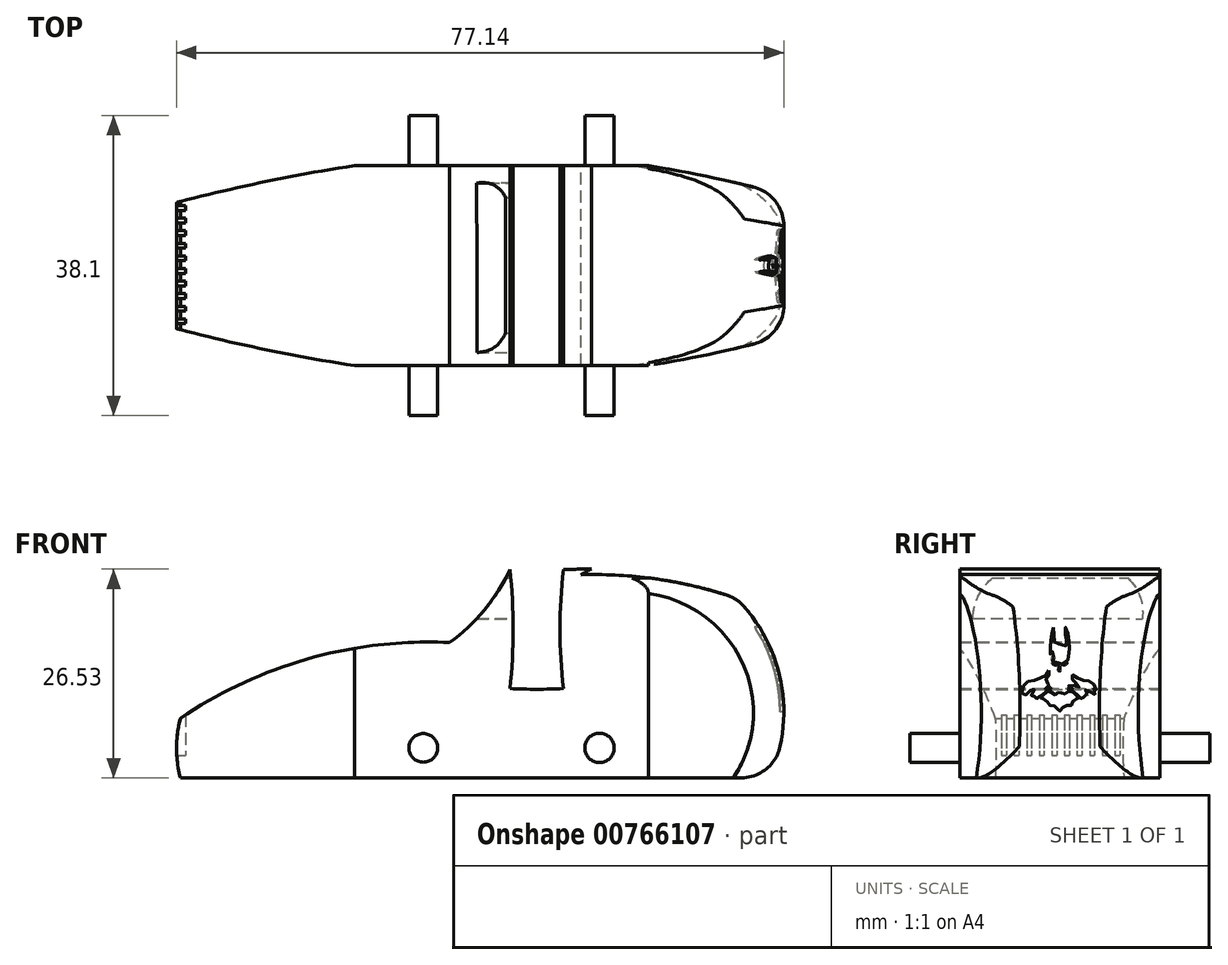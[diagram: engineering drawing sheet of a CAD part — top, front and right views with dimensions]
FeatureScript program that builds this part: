
annotation { "Feature Type Name" : "Feature", "Feature Type Description" : "" }
export const myFeature = defineFeature(function(context is Context, id is Id, definition is map)
    precondition{}
    {
        {
            var Q0;
            Q0=qCreatedBy(makeId("Front.planeOp"),FACE);
            var sketch = newSketch(context, id + "F0", { "sketchPlane" : qUnion([Q0])});
            skLineSegment(sketch, "E0", {"start": v(14.06, 0) * mm, "end": v(-22.7, 0) * mm});
            skLineSegment(sketch, "E1", {"start": v(-22.7, 0) * mm, "end": v(-22.7, 4.32) * mm});
            skArc(sketch, "E2", {"start": v(-6.24, 12.14) * mm, "mid": v(-14.95, 9.24) * mm, "end": v(-22.7, 4.32) * mm});
            skArc(sketch, "E3", {"start": v(-6.24, 12.14) * mm, "mid": v(-3.82, 13.42) * mm, "end": v(-2.13, 15.57) * mm});
            skLineSegment(sketch, "E4", {"start": v(-2.13, 15.57) * mm, "end": v(0, 6.38) * mm});
            skLineSegment(sketch, "E5", {"start": v(0, 6.38) * mm, "end": v(6.51, 6.38) * mm});
            skLineSegment(sketch, "E6", {"start": v(6.51, 6.38) * mm, "end": v(6.51, 15.57) * mm});
            skArc(sketch, "E7", {"start": v(14.06, 0) * mm, "mid": v(14.06, 9.61) * mm, "end": v(6.51, 15.57) * mm});
            skCircle(sketch, "E8", {"center": v(-14.41, 3.81) * mm, "radius": 1.82 * mm});
            skCircle(sketch, "E9", {"center": v(7.97, 3.81) * mm, "radius": 1.86 * mm});
            skSolve(sketch);
        }
        {
            var Q0;
            Q0 = qSketchRegion(id + "F0", true);
            extrude(context, id + "F1", {"entities" : qUnion([Q0]), "endBound" : BoundingType.SYMMETRIC, "depth" : 17.78 * mm, "offsetDistance" : 25.4 * mm});
        }
        {
            var Q0;
            Q0=qCreatedBy(makeId("Top.planeOp"),FACE);
            var sketch = newSketch(context, id + "F2", { "sketchPlane" : qUnion([Q0])});
            skArc(sketch, "E10", {"start": v(0, 11.7) * mm, "mid": v(-18.06, 8.8) * mm, "end": v(-34.94, 1.75) * mm});
            skArc(sketch, "E11", {"start": v(21.66, 0) * mm, "mid": v(12.6, 9.1) * mm, "end": v(0, 11.7) * mm});
            skArc(sketch, "E12.MirrorCS", {"start": v(21.66, 0) * mm, "mid": v(12.6, -9.1) * mm, "end": v(0, -11.7) * mm});
            skArc(sketch, "E13.MirrorCS", {"start": v(0, -11.7) * mm, "mid": v(-18.06, -8.8) * mm, "end": v(-34.94, -1.75) * mm});
            skLineSegment(sketch, "E14", {"start": v(-34.94, -1.75) * mm, "end": v(-25.16, -25.9) * mm});
            skLineSegment(sketch, "E15", {"start": v(-25.16, -25.9) * mm, "end": v(27.75, -24.43) * mm});
            skLineSegment(sketch, "E16", {"start": v(27.75, -24.43) * mm, "end": v(34.75, 13.37) * mm});
            skLineSegment(sketch, "E17", {"start": v(34.75, 13.37) * mm, "end": v(1.57, 21.1) * mm});
            skLineSegment(sketch, "E18", {"start": v(1.57, 21.1) * mm, "end": v(-34.94, 12.44) * mm});
            skLineSegment(sketch, "E19", {"start": v(-34.94, 12.44) * mm, "end": v(-34.94, 1.75) * mm});
            skSolve(sketch);
        }
        {
            var Q0;
            Q0 = qSketchRegion(id + "F2", true);
            extrude(context, id + "F3", {"entities" : qUnion([Q0]), "operationType" : NewBodyOperationType.REMOVE, "depth" : 43.18 * mm, "offsetDistance" : 25.4 * mm});
        }
        {
            var Q0;
            Q0=makeQuery(id+"F1.opExtrude","SWEPT_BODY",BODY,{"disambiguationData":[OSD([sQuery(id+"F0.wireOp",EDGE,"E0"),sQuery(id+"F0.wireOp",EDGE,"E1"),sQuery(id+"F0.wireOp",EDGE,"E2"),sQuery(id+"F0.wireOp",EDGE,"E3"),sQuery(id+"F0.wireOp",EDGE,"E4"),sQuery(id+"F0.wireOp",EDGE,"E5"),sQuery(id+"F0.wireOp",EDGE,"E6"),sQuery(id+"F0.wireOp",EDGE,"E7")])]});
            deleteBodies(context, id + "F4", {"entities" : qUnion([Q0])});
        }
        {
            var Q0;
            Q0=qCreatedBy(makeId("Front.planeOp"),FACE);
            var sketch = newSketch(context, id + "F5", { "sketchPlane" : qUnion([Q0])});
            skArc(sketch, "E20", {"start": v(-11.07, 17.2) * mm, "mid": v(-28.95, 15.15) * mm, "end": v(-45.26, 7.56) * mm});
            skArc(sketch, "E21", {"start": v(-11.07, 17.2) * mm, "mid": v(-6.65, 21.34) * mm, "end": v(-3.41, 26.45) * mm});
            skArc(sketch, "E22", {"start": v(-3.41, 11.34) * mm, "mid": v(-3, 18.9) * mm, "end": v(-3.41, 26.45) * mm});
            skArc(sketch, "E23", {"start": v(-3.41, 11.34) * mm, "mid": v(0, 11.26) * mm, "end": v(3.41, 11.34) * mm});
            skArc(sketch, "E24", {"start": v(3.41, 26.45) * mm, "mid": v(2.95, 18.9) * mm, "end": v(3.41, 11.34) * mm});
            skArc(sketch, "E25", {"start": v(22.77, 24.98) * mm, "mid": v(13.13, 26.29) * mm, "end": v(3.41, 26.45) * mm});
            skArc(sketch, "E26", {"start": v(-45.26, 7.56) * mm, "mid": v(-45.76, 3.78) * mm, "end": v(-45.26, 0) * mm});
            skArc(sketch, "E27", {"start": v(29.59, 0) * mm, "mid": v(30.66, 13.71) * mm, "end": v(22.77, 24.98) * mm});
            skLineSegment(sketch, "E28", {"start": v(-45.26, 0) * mm, "end": v(29.59, 0) * mm});
            skLineSegment(sketch, "E29", {"start": v(-3.41, 11.34) * mm, "end": v(0, 0) * mm, "construction": true});
            skLineSegment(sketch, "E30", {"start": v(0, 0) * mm, "end": v(3.41, 11.34) * mm, "construction": true});
            skSolve(sketch);
        }
        {
            var Q0;
            Q0=makeQuery(id+"F5.imprint","IMPRINT",FACE,{"disambiguationData":[TD([[makeQuery(id+"F5.imprint","IMPRINT",EDGE,{"derivedFrom":sQuery(id+"F5.wireOp",EDGE,"E20")}),1.0]])]});
            extrude(context, id + "F6", {"entities" : qUnion([Q0]), "endBound" : BoundingType.SYMMETRIC, "depth" : 25.4 * mm, "offsetDistance" : 25.4 * mm});
        }
        {
            var Q0;
            Q0=qCreatedBy(makeId("Top.planeOp"),FACE);
            var sketch = newSketch(context, id + "F7", { "sketchPlane" : qUnion([Q0])});
            skArc(sketch, "E31", {"start": v(-5.44, 14.66) * mm, "mid": v(-27.48, 12) * mm, "end": v(-49.13, 7.1) * mm});
            skArc(sketch, "E32", {"start": v(38.25, 6.91) * mm, "mid": v(16.67, 12.28) * mm, "end": v(-5.44, 14.66) * mm});
            skArc(sketch, "E33.MirrorCS", {"start": v(38.25, -6.91) * mm, "mid": v(16.67, -12.28) * mm, "end": v(-5.44, -14.66) * mm});
            skArc(sketch, "E34.MirrorCS", {"start": v(-5.44, -14.66) * mm, "mid": v(-27.48, -12) * mm, "end": v(-49.13, -7.1) * mm});
            skLineSegment(sketch, "E35", {"start": v(-50.05, 21.85) * mm, "end": v(24.06, 21.85) * mm});
            skLineSegment(sketch, "E36", {"start": v(24.06, 21.85) * mm, "end": v(58.53, 12.81) * mm});
            skLineSegment(sketch, "E37", {"start": v(58.53, 12.81) * mm, "end": v(58.53, -6.36) * mm});
            skLineSegment(sketch, "E38", {"start": v(58.53, -6.36) * mm, "end": v(36.23, -29.4) * mm});
            skLineSegment(sketch, "E39", {"start": v(36.23, -29.4) * mm, "end": v(-53.37, -29.4) * mm});
            skLineSegment(sketch, "E40", {"start": v(-53.37, -29.4) * mm, "end": v(-69.96, 0) * mm});
            skLineSegment(sketch, "E41", {"start": v(-69.96, 0) * mm, "end": v(-50.05, 21.85) * mm});
            skLineSegment(sketch, "E42", {"start": v(-49.13, 7.1) * mm, "end": v(-49.13, -7.1) * mm});
            skLineSegment(sketch, "E43", {"start": v(38.25, 6.91) * mm, "end": v(38.25, -6.91) * mm});
            skSolve(sketch);
        }
        {
            var Q0;
            Q0=makeQuery(id+"F7.imprint","IMPRINT",FACE,{"disambiguationData":[TD([[makeQuery(id+"F7.imprint","IMPRINT",EDGE,{"derivedFrom":sQuery(id+"F7.wireOp",EDGE,"E31")}),-1.0]])]});
            extrude(context, id + "F8", {"entities" : qUnion([Q0]), "operationType" : NewBodyOperationType.REMOVE, "depth" : 25.4 * mm, "offsetDistance" : 25.4 * mm});
        }
        {
            var Q0;
            Q0=makeQuery(id+"F0.imprint","IMPRINT",FACE,{"disambiguationData":[TD([[makeQuery(id+"F0.imprint","IMPRINT",EDGE,{"derivedFrom":sQuery(id+"F0.wireOp",EDGE,"E9")}),1.0]])]});
            var Q1;
            Q1=makeQuery(id+"F0.imprint","IMPRINT",FACE,{"disambiguationData":[TD([[makeQuery(id+"F0.imprint","IMPRINT",EDGE,{"derivedFrom":sQuery(id+"F0.wireOp",EDGE,"E8")}),1.0]])]});
            extrude(context, id + "F9", {"entities" : qUnion([Q0, Q1]), "operationType" : NewBodyOperationType.ADD, "endBound" : BoundingType.SYMMETRIC, "depth" : 38.1 * mm, "offsetDistance" : 25.4 * mm});
        }
        {
            var Q0;
            Q0=qCreatedBy(makeId("Right.planeOp"),FACE);
            var sketch = newSketch(context, id + "F10", { "sketchPlane" : qUnion([Q0])});
            skArc(sketch, "E44", {"start": v(10.48, 20.22) * mm, "mid": v(10.2, 23.02) * mm, "end": v(8.66, 25.37) * mm});
            skArc(sketch, "E45", {"start": v(-8.55, 25.37) * mm, "mid": v(-10.34, 23.1) * mm, "end": v(-11.03, 20.28) * mm});
            skLineSegment(sketch, "E46", {"start": v(8.66, 25.37) * mm, "end": v(-8.55, 25.37) * mm});
            skLineSegment(sketch, "E47", {"start": v(10.48, 20.22) * mm, "end": v(-11.03, 20.28) * mm});
            skSolve(sketch);
        }
        {
            var Q0;
            Q0=makeQuery(id+"F10.imprint","IMPRINT",FACE,{"disambiguationData":[TD([[makeQuery(id+"F10.imprint","IMPRINT",EDGE,{"derivedFrom":sQuery(id+"F10.wireOp",EDGE,"E44")}),1.0]])]});
            extrude(context, id + "F11", {"entities" : qUnion([Q0]), "operationType" : NewBodyOperationType.REMOVE, "oppositeDirection" : true, "depth" : 7.65 * mm, "offsetDistance" : 25.4 * mm});
        }
        {
            var Q0;
            Q0=qCreatedBy(makeId("Right.planeOp"),FACE);
            var sketch = newSketch(context, id + "F12", { "sketchPlane" : qUnion([Q0])});
            skFitSpline(sketch, "E48", {"points": [v(-0.82, 19.14) * mm, v(-0.88, 19.02) * mm, v(-0.93, 18.82) * mm, v(-0.98, 18.55) * mm, v(-1.04, 18.17) * mm, v(-1.1, 17.77) * mm, v(-1.15, 17.25) * mm, v(-1.18, 16.87) * mm, v(-1.21, 16.4) * mm, v(-1.24, 15.96) * mm, v(-1.1, 15.47) * mm, v(-1.02, 15.47) * mm, v(-1, 15.57) * mm, v(-0.93, 15.95) * mm, v(-0.9, 16.05) * mm, v(-0.9, 15.74) * mm, v(-0.89, 15.43) * mm, v(-0.82, 15.34) * mm, v(-0.74, 15.1) * mm, v(-0.95, 15.18) * mm, v(-1.03, 15.17) * mm, v(-1.04, 14.83) * mm, v(-0.94, 14.78) * mm, v(-0.55, 14.58) * mm, v(-0.3, 14.47) * mm, v(-0.16, 14.47) * mm, v(-0.15, 14.64) * mm, v(-0.07, 14.6) * mm, v(0, 14.56) * mm, v(0.07, 14.58) * mm, v(0.07, 14.71) * mm, v(0.13, 14.73) * mm, v(0.17, 14.46) * mm, v(0.36, 14.55) * mm, v(0.64, 14.72) * mm, v(1.02, 14.83) * mm, v(1.03, 15.1) * mm, v(1.1, 15.43) * mm, v(1.17, 15.68) * mm, v(1.13, 16) * mm, v(1.08, 16.14) * mm, v(1.05, 16.2) * mm, v(1.05, 16.32) * mm, v(1.07, 16.35) * mm, v(1.11, 16.33) * mm, v(1.13, 16.27) * mm, v(1.2, 16.19) * mm, v(1.25, 16.2) * mm, v(1.25, 16.36) * mm, v(1.2, 17.1) * mm, v(1.16, 17.6) * mm, v(1.05, 18.23) * mm, v(0.89, 18.87) * mm, v(0.77, 19.15) * mm, v(0.74, 19.16) * mm, v(0.74, 18.89) * mm, v(0.74, 17.91) * mm, v(0.74, 17.66) * mm, v(0.73, 17.52) * mm, v(0.75, 17.44) * mm, v(0.82, 17.44) * mm, v(0.85, 17.54) * mm, v(0.85, 17.62) * mm, v(0.87, 17.74) * mm, v(0.88, 17.87) * mm, v(0.86, 18.02) * mm, v(0.88, 18.11) * mm, v(0.93, 18.02) * mm, v(0.93, 17.9) * mm, v(0.94, 17.73) * mm, v(0.92, 17.57) * mm, v(0.9, 17.4) * mm, v(0.9, 17.24) * mm, v(0.89, 17.1) * mm, v(0.78, 16.73) * mm, v(0.77, 16.68) * mm, v(0.56, 16.86) * mm, v(0.32, 16.97) * mm, v(0, 17.02) * mm, v(-0.31, 17) * mm, v(-0.63, 16.88) * mm, v(-0.67, 17.49) * mm, v(-0.7, 18.14) * mm, v(-0.82, 19.14) * mm]});
            skFitSpline(sketch, "E49", {"points": [v(-0.9, 14.63) * mm, v(-0.93, 14.6) * mm, v(-0.9, 14.53) * mm, v(-0.83, 14.44) * mm, v(-0.79, 14.4) * mm, v(-0.7, 14.36) * mm, v(-0.59, 14.35) * mm, v(-0.53, 14.36) * mm, v(-0.5, 14.32) * mm, v(-0.44, 14.3) * mm, v(-0.4, 14.36) * mm, v(-0.4, 14.43) * mm, v(-0.41, 14.45) * mm, v(-0.48, 14.46) * mm, v(-0.55, 14.5) * mm, v(-0.66, 14.56) * mm, v(-0.84, 14.65) * mm, v(-0.9, 14.63) * mm]});
            skFitSpline(sketch, "E50", {"points": [v(0, 14.23) * mm, v(-0.07, 14.21) * mm, v(-0.07, 14.1) * mm, v(-0.12, 13.98) * mm, v(-0.12, 13.9) * mm, v(-0.16, 13.83) * mm, v(-0.17, 13.77) * mm, v(-0.17, 13.71) * mm, v(-0.16, 13.66) * mm, v(-0.12, 13.6) * mm, v(-0.07, 13.57) * mm, v(0.04, 13.56) * mm, v(0.06, 13.6) * mm, v(0.06, 13.7) * mm, v(0.04, 13.76) * mm, v(0.04, 13.83) * mm, v(0.04, 13.93) * mm, v(0.04, 13.99) * mm, v(0.04, 14.1) * mm, v(0.04, 14.15) * mm, v(0.04, 14.2) * mm, v(0, 14.23) * mm]});
            skFitSpline(sketch, "E51", {"points": [v(0.36, 14.38) * mm, v(0.4, 14.36) * mm, v(0.45, 14.36) * mm, v(0.56, 14.35) * mm, v(0.62, 14.35) * mm, v(0.71, 14.37) * mm, v(0.76, 14.4) * mm, v(0.83, 14.46) * mm, v(0.9, 14.52) * mm, v(0.94, 14.57) * mm, v(0.95, 14.6) * mm, v(0.9, 14.65) * mm, v(0.86, 14.65) * mm, v(0.74, 14.6) * mm, v(0.63, 14.54) * mm, v(0.53, 14.46) * mm, v(0.5, 14.46) * mm, v(0.43, 14.46) * mm, v(0.36, 14.38) * mm]});
            skFitSpline(sketch, "E52", {"points": [v(-1.4, 13.67) * mm, v(-1.43, 13.45) * mm, v(-1.45, 13.3) * mm, v(-1.5, 13.18) * mm, v(-1.66, 13.08) * mm, v(-2.08, 12.86) * mm, v(-3.23, 12.38) * mm, v(-3.34, 12.39) * mm, v(-3.5, 12.38) * mm, v(-3.72, 12.33) * mm, v(-4, 12.24) * mm, v(-4.37, 11.96) * mm, v(-4.53, 11.77) * mm, v(-4.67, 11.52) * mm, v(-4.75, 11.19) * mm, v(-4.77, 10.94) * mm, v(-4.78, 10.87) * mm, v(-4.67, 11.02) * mm, v(-4.6, 11.15) * mm, v(-4.58, 10.95) * mm, v(-4.58, 10.76) * mm, v(-4.58, 10.54) * mm, v(-4.52, 10.27) * mm, v(-4.44, 10.32) * mm, v(-4.32, 10.47) * mm, v(-4.09, 10.74) * mm, v(-3.7, 11.1) * mm, v(-3.45, 11.29) * mm, v(-3.24, 11.4) * mm, v(-3.16, 11.38) * mm, v(-3.18, 11.27) * mm, v(-3.37, 11) * mm, v(-3.57, 10.62) * mm, v(-3.6, 10.46) * mm, v(-3.57, 10.4) * mm, v(-3.46, 10.5) * mm, v(-3.25, 10.6) * mm, v(-3.18, 10.61) * mm, v(-3.18, 10.52) * mm, v(-3.24, 10.38) * mm, v(-3.3, 10.22) * mm, v(-3.3, 10.1) * mm, v(-3.23, 10.05) * mm, v(-3.16, 10.17) * mm, v(-3.04, 10.22) * mm, v(-3, 10.22) * mm, v(-2.97, 10.15) * mm, v(-2.97, 10.03) * mm, v(-2.95, 9.93) * mm, v(-2.87, 9.91) * mm, v(-2.7, 10.14) * mm, v(-2.37, 10.47) * mm, v(-1.83, 10.87) * mm, v(-1.43, 11.1) * mm, v(-0.93, 11.36) * mm, v(-0.8, 11.38) * mm, v(-0.8, 11.45) * mm, v(-0.97, 11.5) * mm, v(-1.17, 11.52) * mm, v(-1.73, 11.24) * mm, v(-1.82, 11.19) * mm, v(-1.86, 11.18) * mm, v(-1.84, 11.29) * mm, v(-1.5, 11.54) * mm, v(-1.28, 11.73) * mm, v(-1.26, 11.78) * mm, v(-1.41, 11.76) * mm, v(-1.64, 11.65) * mm, v(-1.75, 11.62) * mm, v(-1.79, 11.68) * mm, v(-1.55, 11.87) * mm, v(-1.38, 12.07) * mm, v(-1.4, 12.22) * mm, v(-1.5, 12.3) * mm, v(-1.54, 12.36) * mm, v(-1.54, 12.48) * mm, v(-1.59, 12.51) * mm, v(-1.74, 12.56) * mm, v(-1.88, 12.54) * mm, v(-1.87, 12.67) * mm, v(-1.68, 12.81) * mm, v(-1.4, 12.98) * mm, v(-1.24, 13.1) * mm, v(-1.28, 13.3) * mm, v(-1.32, 13.5) * mm, v(-1.3, 13.67) * mm, v(-1.34, 13.71) * mm, v(-1.4, 13.67) * mm]});
            skFitSpline(sketch, "E53", {"points": [v(-0.23, 10.87) * mm, v(-0.18, 10.83) * mm, v(-0.07, 10.81) * mm, v(0.04, 10.82) * mm, v(0.12, 10.84) * mm, v(0.17, 10.86) * mm, v(0.21, 10.9) * mm, v(0.23, 10.8) * mm, v(0.23, 10.7) * mm, v(0.26, 10.62) * mm, v(0.3, 10.58) * mm, v(0.39, 10.57) * mm, v(0.5, 10.58) * mm, v(0.61, 10.64) * mm, v(0.77, 10.7) * mm, v(0.87, 10.78) * mm, v(1, 10.88) * mm, v(1.1, 11) * mm, v(1.19, 11.1) * mm, v(1.24, 11.16) * mm, v(1.38, 11.12) * mm, v(1.51, 11.02) * mm, v(1.68, 10.89) * mm, v(1.85, 10.76) * mm, v(1.98, 10.64) * mm, v(2.08, 10.54) * mm, v(2.2, 10.4) * mm, v(2.34, 10.24) * mm, v(2.47, 10.1) * mm, v(2.52, 10.03) * mm, v(2.46, 10.03) * mm, v(2.34, 10.02) * mm, v(2.16, 10) * mm, v(2, 9.97) * mm, v(1.9, 9.92) * mm, v(1.76, 9.82) * mm, v(1.68, 9.72) * mm, v(1.63, 9.62) * mm, v(1.57, 9.53) * mm, v(1.54, 9.43) * mm, v(1.5, 9.33) * mm, v(1.48, 9.23) * mm, v(1.46, 9.17) * mm, v(1.34, 9.2) * mm, v(1.19, 9.23) * mm, v(1.04, 9.23) * mm, v(0.83, 9.22) * mm, v(0.67, 9.19) * mm, v(0.55, 9.13) * mm, v(0.45, 9.04) * mm, v(0.34, 8.93) * mm, v(0.25, 8.81) * mm, v(0.17, 8.68) * mm, v(0.07, 8.5) * mm, v(0, 8.38) * mm, v(0, 8.36) * mm, v(-0.07, 8.4) * mm, v(-0.15, 8.53) * mm, v(-0.24, 8.67) * mm, v(-0.32, 8.82) * mm, v(-0.4, 8.92) * mm, v(-0.5, 9) * mm, v(-0.65, 9.12) * mm, v(-0.76, 9.18) * mm, v(-0.96, 9.22) * mm, v(-1.13, 9.24) * mm, v(-1.28, 9.22) * mm, v(-1.38, 9.22) * mm, v(-1.42, 9.34) * mm, v(-1.46, 9.46) * mm, v(-1.53, 9.56) * mm, v(-1.64, 9.73) * mm, v(-1.74, 9.85) * mm, v(-1.88, 9.93) * mm, v(-2.1, 10) * mm, v(-2.33, 10.01) * mm, v(-2.5, 10) * mm, v(-2.4, 10.16) * mm, v(-2.25, 10.37) * mm, v(-2.06, 10.55) * mm, v(-1.9, 10.7) * mm, v(-1.66, 10.85) * mm, v(-1.44, 10.99) * mm, v(-1.2, 11.12) * mm, v(-1.18, 11.08) * mm, v(-1.13, 10.99) * mm, v(-1.05, 10.88) * mm, v(-1, 10.78) * mm, v(-0.89, 10.68) * mm, v(-0.77, 10.6) * mm, v(-0.63, 10.56) * mm, v(-0.46, 10.54) * mm, v(-0.31, 10.54) * mm, v(-0.28, 10.62) * mm, v(-0.24, 10.72) * mm, v(-0.23, 10.87) * mm]});
            skFitSpline(sketch, "E54", {"points": [v(0.95, 11.4) * mm, v(1.22, 11.28) * mm, v(1.45, 11.17) * mm, v(1.68, 11.02) * mm, v(1.93, 10.83) * mm, v(2.2, 10.6) * mm, v(2.5, 10.3) * mm, v(2.63, 10.16) * mm, v(2.76, 10) * mm, v(2.81, 9.92) * mm, v(2.87, 9.88) * mm, v(2.93, 9.92) * mm, v(2.97, 9.98) * mm, v(3.02, 10.04) * mm, v(3.04, 10.11) * mm, v(3.03, 10.27) * mm, v(3.02, 10.33) * mm, v(3.06, 10.36) * mm, v(3.15, 10.36) * mm, v(3.25, 10.37) * mm, v(3.26, 10.4) * mm, v(3.18, 10.51) * mm, v(3.19, 10.57) * mm, v(3.34, 10.54) * mm, v(3.57, 10.49) * mm, v(3.66, 10.46) * mm, v(3.66, 10.54) * mm, v(3.6, 10.64) * mm, v(3.52, 10.74) * mm, v(3.43, 10.84) * mm, v(3.32, 10.94) * mm, v(3.2, 11.05) * mm, v(3.13, 11.13) * mm, v(3.09, 11.18) * mm, v(3.23, 11.2) * mm, v(3.47, 11.12) * mm, v(3.73, 11.03) * mm, v(3.96, 10.93) * mm, v(4.2, 10.78) * mm, v(4.32, 10.7) * mm, v(4.4, 10.6) * mm, v(4.43, 10.56) * mm, v(4.43, 10.74) * mm, v(4.42, 10.95) * mm, v(4.39, 11.15) * mm, v(4.36, 11.33) * mm, v(4.35, 11.37) * mm, v(4.46, 11.3) * mm, v(4.57, 11.1) * mm, v(4.6, 11) * mm, v(4.6, 11.33) * mm, v(4.54, 11.53) * mm, v(4.43, 11.75) * mm, v(4.3, 11.94) * mm, v(4.11, 12.1) * mm, v(3.87, 12.24) * mm, v(3.64, 12.3) * mm, v(3.4, 12.37) * mm, v(3.2, 12.37) * mm, v(3, 12.38) * mm, v(2.85, 12.43) * mm, v(2.62, 12.5) * mm, v(2.42, 12.6) * mm, v(2.15, 12.74) * mm, v(1.88, 12.9) * mm, v(1.62, 13.05) * mm, v(1.6, 13.06) * mm, v(1.55, 13.06) * mm, v(1.55, 13.03) * mm, v(1.56, 12.97) * mm, v(1.58, 12.95) * mm, v(1.57, 12.9) * mm, v(1.54, 12.87) * mm, v(1.54, 12.82) * mm, v(1.56, 12.77) * mm, v(1.57, 12.72) * mm, v(1.51, 12.68) * mm, v(1.51, 12.6) * mm, v(1.53, 12.55) * mm, v(1.63, 12.5) * mm, v(1.75, 12.4) * mm, v(1.8, 12.37) * mm, v(1.8, 12.32) * mm, v(1.76, 12.3) * mm, v(1.71, 12.3) * mm, v(1.66, 12.29) * mm, v(1.71, 12.26) * mm, v(1.85, 12.17) * mm, v(2.03, 12.07) * mm, v(2.2, 11.94) * mm, v(2.32, 11.83) * mm, v(2.4, 11.7) * mm, v(2.45, 11.55) * mm, v(2.44, 11.49) * mm, v(2.37, 11.47) * mm, v(2.23, 11.48) * mm, v(2.14, 11.54) * mm, v(1.97, 11.63) * mm, v(1.74, 11.75) * mm, v(1.5, 11.8) * mm, v(1.31, 11.8) * mm, v(1.17, 11.78) * mm, v(1.1, 11.75) * mm, v(1.15, 11.68) * mm, v(1.29, 11.61) * mm, v(1.44, 11.54) * mm, v(1.58, 11.47) * mm, v(1.67, 11.4) * mm, v(1.71, 11.36) * mm, v(1.72, 11.35) * mm, v(1.72, 11.33) * mm, v(1.7, 11.32) * mm, v(1.62, 11.36) * mm, v(1.5, 11.4) * mm, v(1.38, 11.44) * mm, v(1.2, 11.48) * mm, v(1.02, 11.48) * mm, v(0.92, 11.44) * mm, v(0.9, 11.42) * mm, v(0.95, 11.4) * mm]});
            skSolve(sketch);
        }
        {
            var Q0;
            Q0 = qSketchRegion(id + "F12", true);
            extrude(context, id + "F13", {"entities" : qUnion([Q0]), "operationType" : NewBodyOperationType.REMOVE, "depth" : 50.72 * mm, "offsetDistance" : 25.4 * mm});
        }
        {
            var Q0;
            Q0=qCreatedBy(makeId("Front.planeOp"),FACE);
            var sketch = newSketch(context, id + "F14", { "sketchPlane" : qUnion([Q0])});
            skArc(sketch, "E55.0", {"start": v(3.41, 26.45) * mm, "mid": v(2.95, 18.9) * mm, "end": v(3.41, 11.34) * mm});
            skArc(sketch, "E56.0", {"start": v(20.46, 25.4) * mm, "mid": v(11.96, 26.37) * mm, "end": v(3.41, 26.45) * mm});
            skArc(sketch, "E57.0", {"start": v(23.3, 23.95) * mm, "mid": v(30, 14.2) * mm, "end": v(29.95, 2.38) * mm});
            skArc(sketch, "E58", {"start": v(23.3, 23.95) * mm, "mid": v(21.96, 24.84) * mm, "end": v(20.46, 25.4) * mm});
            skArc(sketch, "E59.0", {"start": v(-3.41, 11.34) * mm, "mid": v(0, 11.26) * mm, "end": v(3.41, 11.34) * mm});
            skLineSegment(sketch, "E60", {"start": v(-3.41, 11.34) * mm, "end": v(-3.41, 7.95) * mm});
            skLineSegment(sketch, "E61", {"start": v(-3.41, 7.95) * mm, "end": v(29.95, 2.38) * mm});
            skSolve(sketch);
        }
        {
            var Q0;
            Q0 = qSketchRegion(id + "F14", true);
            extrude(context, id + "F15", {"entities" : qUnion([Q0]), "operationType" : NewBodyOperationType.ADD, "endBound" : BoundingType.SYMMETRIC, "depth" : 15.8 * mm, "offsetDistance" : 25.4 * mm});
        }
        {
            var Q0;
            Q0=qCreatedBy(makeId("Right.planeOp"),FACE);
            cPlane(context, id + "F16", {"entities" : qUnion([Q0]), "cplaneType" : CPlaneType.OFFSET, "offset" : 44.6 * mm, "oppositeDirection" : true, "width" : 152.4 * mm, "height" : 152.4 * mm});
        }
        {
            var Q0;
            Q0=qCreatedBy(id+"F16.planeOp",FACE);
            var sketch = newSketch(context, id + "F17", { "sketchPlane" : qUnion([Q0])});
            skLineSegment(sketch, "E62.bottom", {"start": v(7.62, 10.4) * mm, "end": v(7.01, 10.4) * mm});
            skLineSegment(sketch, "E62.top", {"start": v(7.62, 2.85) * mm, "end": v(7.01, 2.85) * mm});
            skLineSegment(sketch, "E62.left", {"start": v(7.62, 10.4) * mm, "end": v(7.62, 2.85) * mm});
            skLineSegment(sketch, "E62.right", {"start": v(7.01, 10.4) * mm, "end": v(7.01, 2.85) * mm});
            skLineSegment(sketch, "E63.1.0.0", {"start": v(5.41, 10.4) * mm, "end": v(5.41, 2.85) * mm});
            skLineSegment(sketch, "E63.1.0.1", {"start": v(6.02, 10.4) * mm, "end": v(6.02, 2.85) * mm});
            skLineSegment(sketch, "E63.1.0.2", {"start": v(6.02, 10.4) * mm, "end": v(5.41, 10.4) * mm});
            skLineSegment(sketch, "E63.1.0.3", {"start": v(6.02, 2.85) * mm, "end": v(5.41, 2.85) * mm});
            skLineSegment(sketch, "E63.2.0.0", {"start": v(3.81, 10.4) * mm, "end": v(3.81, 2.85) * mm});
            skLineSegment(sketch, "E63.2.0.1", {"start": v(4.42, 10.4) * mm, "end": v(4.42, 2.85) * mm});
            skLineSegment(sketch, "E63.2.0.2", {"start": v(4.42, 10.4) * mm, "end": v(3.81, 10.4) * mm});
            skLineSegment(sketch, "E63.2.0.3", {"start": v(4.42, 2.85) * mm, "end": v(3.81, 2.85) * mm});
            skLineSegment(sketch, "E63.3.0.0", {"start": v(2.21, 10.4) * mm, "end": v(2.21, 2.85) * mm});
            skLineSegment(sketch, "E63.3.0.1", {"start": v(2.82, 10.4) * mm, "end": v(2.82, 2.85) * mm});
            skLineSegment(sketch, "E63.3.0.2", {"start": v(2.82, 10.4) * mm, "end": v(2.21, 10.4) * mm});
            skLineSegment(sketch, "E63.3.0.3", {"start": v(2.82, 2.85) * mm, "end": v(2.21, 2.85) * mm});
            skLineSegment(sketch, "E63.4.0.0", {"start": v(0.61, 10.4) * mm, "end": v(0.61, 2.85) * mm});
            skLineSegment(sketch, "E63.4.0.1", {"start": v(1.22, 10.4) * mm, "end": v(1.22, 2.85) * mm});
            skLineSegment(sketch, "E63.4.0.2", {"start": v(1.22, 10.4) * mm, "end": v(0.61, 10.4) * mm});
            skLineSegment(sketch, "E63.4.0.3", {"start": v(1.22, 2.85) * mm, "end": v(0.61, 2.85) * mm});
            skLineSegment(sketch, "E63.5.0.0", {"start": v(-0.99, 10.4) * mm, "end": v(-0.99, 2.85) * mm});
            skLineSegment(sketch, "E63.5.0.1", {"start": v(-0.38, 10.4) * mm, "end": v(-0.38, 2.85) * mm});
            skLineSegment(sketch, "E63.5.0.2", {"start": v(-0.38, 10.4) * mm, "end": v(-0.99, 10.4) * mm});
            skLineSegment(sketch, "E63.5.0.3", {"start": v(-0.38, 2.85) * mm, "end": v(-0.99, 2.85) * mm});
            skLineSegment(sketch, "E63.6.0.0", {"start": v(-2.6, 10.4) * mm, "end": v(-2.6, 2.85) * mm});
            skLineSegment(sketch, "E63.6.0.1", {"start": v(-1.98, 10.4) * mm, "end": v(-1.98, 2.85) * mm});
            skLineSegment(sketch, "E63.6.0.2", {"start": v(-1.98, 10.4) * mm, "end": v(-2.6, 10.4) * mm});
            skLineSegment(sketch, "E63.6.0.3", {"start": v(-1.98, 2.85) * mm, "end": v(-2.6, 2.85) * mm});
            skLineSegment(sketch, "E63.7.0.0", {"start": v(-4.2, 10.4) * mm, "end": v(-4.2, 2.85) * mm});
            skLineSegment(sketch, "E63.7.0.1", {"start": v(-3.58, 10.4) * mm, "end": v(-3.58, 2.85) * mm});
            skLineSegment(sketch, "E63.7.0.2", {"start": v(-3.58, 10.4) * mm, "end": v(-4.2, 10.4) * mm});
            skLineSegment(sketch, "E63.7.0.3", {"start": v(-3.58, 2.85) * mm, "end": v(-4.2, 2.85) * mm});
            skLineSegment(sketch, "E63.8.0.0", {"start": v(-5.8, 10.4) * mm, "end": v(-5.8, 2.85) * mm});
            skLineSegment(sketch, "E63.8.0.1", {"start": v(-5.18, 10.4) * mm, "end": v(-5.18, 2.85) * mm});
            skLineSegment(sketch, "E63.8.0.2", {"start": v(-5.18, 10.4) * mm, "end": v(-5.8, 10.4) * mm});
            skLineSegment(sketch, "E63.8.0.3", {"start": v(-5.18, 2.85) * mm, "end": v(-5.8, 2.85) * mm});
            skLineSegment(sketch, "E63.9.0.0", {"start": v(-7.4, 10.4) * mm, "end": v(-7.4, 2.85) * mm});
            skLineSegment(sketch, "E63.9.0.1", {"start": v(-6.78, 10.4) * mm, "end": v(-6.78, 2.85) * mm});
            skLineSegment(sketch, "E63.9.0.2", {"start": v(-6.78, 10.4) * mm, "end": v(-7.4, 10.4) * mm});
            skLineSegment(sketch, "E63.9.0.3", {"start": v(-6.78, 2.85) * mm, "end": v(-7.4, 2.85) * mm});
            skLineSegment(sketch, "E63.direction1", {"start": v(7.01, 2.85) * mm, "end": v(5.41, 2.85) * mm, "construction": true});
            skSolve(sketch);
        }
        {
            var Q0;
            Q0 = qSketchRegion(id + "F17", true);
            extrude(context, id + "F18", {"entities" : qUnion([Q0]), "operationType" : NewBodyOperationType.REMOVE, "oppositeDirection" : true, "depth" : 25.4 * mm, "offsetDistance" : 25.4 * mm});
        }
        {
            var Q0;
            Q0=qCreatedBy(makeId("Front.planeOp"),FACE);
            var sketch = newSketch(context, id + "F19", { "sketchPlane" : qUnion([Q0])});
            skArc(sketch, "E64", {"start": v(44.67, 11.35) * mm, "mid": v(26.55, 22.4) * mm, "end": v(5.6, 25.8) * mm});
            skArc(sketch, "E65", {"start": v(33.53, 27.63) * mm, "mid": v(19.35, 29.97) * mm, "end": v(5.6, 25.8) * mm});
            skArc(sketch, "E66", {"start": v(44.67, 11.35) * mm, "mid": v(40.04, 20.13) * mm, "end": v(33.53, 27.63) * mm});
            skSolve(sketch);
        }
        {
            var Q0;
            Q0=makeQuery(id+"F19.imprint","IMPRINT",FACE,{"disambiguationData":[TD([[makeQuery(id+"F19.imprint","IMPRINT",EDGE,{"derivedFrom":sQuery(id+"F19.wireOp",EDGE,"E64")}),-1.0]])]});
            extrude(context, id + "F20", {"entities" : qUnion([Q0]), "operationType" : NewBodyOperationType.REMOVE, "endBound" : BoundingType.SYMMETRIC, "depth" : 64.52 * mm, "offsetDistance" : 25.4 * mm});
        }
        {
            var Q0;
            Q0=makeQuery(id+"F8.boolean.opBoolean","INTERSECT",EDGE,{"derivedFrom":[makeQuery(id+"F6.opExtrude","SWEPT_FACE",FACE,{"disambiguationData":[OSD([sQuery(id+"F5.wireOp",EDGE,"E27")])]}),makeQuery(id+"F8.opExtrude","SWEPT_FACE",FACE,{"disambiguationData":[OSD([sQuery(id+"F7.wireOp",EDGE,"E33.MirrorCS")])]})]});
            var Q1;
            Q1=makeQuery(id+"F20.boolean.opBoolean","INTERSECT",EDGE,{"derivedFrom":[makeQuery(id+"F6.opExtrude","SWEPT_FACE",FACE,{"disambiguationData":[OSD([sQuery(id+"F5.wireOp",EDGE,"E27")])]}),makeQuery(id+"F20.opExtrude","SWEPT_FACE",FACE,{"disambiguationData":[OSD([sQuery(id+"F19.wireOp",EDGE,"E64")])]})]});
            var Q2;
            Q2=makeQuery(id+"F8.boolean.opBoolean","INTERSECT",EDGE,{"derivedFrom":[makeQuery(id+"F6.opExtrude","SWEPT_FACE",FACE,{"disambiguationData":[OSD([sQuery(id+"F5.wireOp",EDGE,"E27")])]}),makeQuery(id+"F8.opExtrude","SWEPT_FACE",FACE,{"disambiguationData":[OSD([sQuery(id+"F7.wireOp",EDGE,"E32")])]})]});
            var Q3;
            Q3=makeQuery(id+"F6.opExtrude","SWEPT_EDGE",EDGE,{"disambiguationData":[OSD([sQuery(id+"F5.wireOp",EDGE,"E27"),sQuery(id+"F5.wireOp",EDGE,"E28")])]});
            fillet(context, id + "F21", {"entities" : qUnion([Q0, Q1, Q2, Q3]), "radius" : 5.08 * mm, "tangentPropagation" : true, "allowEdgeOverflow" : false});
        }
    });
